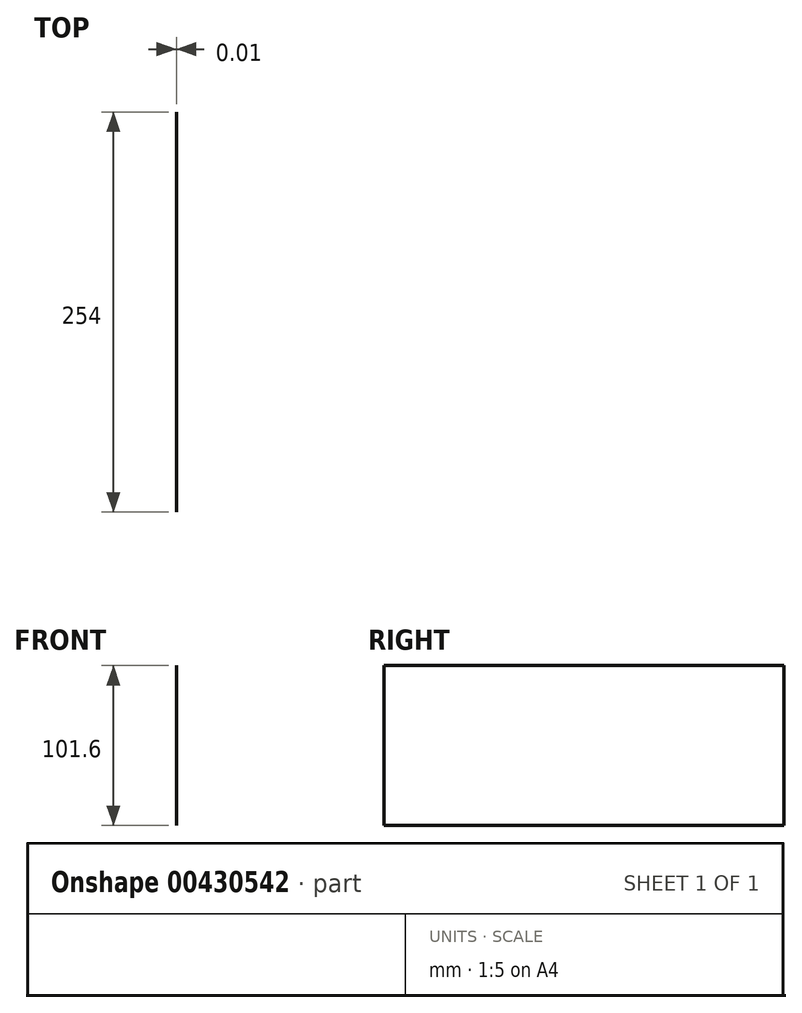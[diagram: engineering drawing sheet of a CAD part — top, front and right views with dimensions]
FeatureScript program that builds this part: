
annotation { "Feature Type Name" : "Feature", "Feature Type Description" : "" }
export const myFeature = defineFeature(function(context is Context, id is Id, definition is map)
    precondition{}
    {
        {
            var Q0;
            Q0=qCreatedBy(makeId("Right.planeOp"),FACE);
            var sketch = newSketch(context, id + "F0", { "sketchPlane" : qUnion([Q0])});
            skLineSegment(sketch, "E0.bottom", {"start": v(-109.97, 63.47) * mm, "end": v(144.03, 63.47) * mm});
            skLineSegment(sketch, "E0.top", {"start": v(-109.97, -38.13) * mm, "end": v(144.03, -38.13) * mm});
            skLineSegment(sketch, "E0.left", {"start": v(-109.97, 63.47) * mm, "end": v(-109.97, -38.13) * mm});
            skLineSegment(sketch, "E0.right", {"start": v(144.03, 63.47) * mm, "end": v(144.03, -38.13) * mm});
            skSolve(sketch);
        }
        {
            var Q0;
            Q0=makeQuery(id+"F0.imprint","IMPRINT",FACE,{"disambiguationData":[TD([[makeQuery(id+"F0.imprint","IMPRINT",EDGE,{"derivedFrom":sQuery(id+"F0.wireOp",EDGE,"E0.bottom")}),-1.0]])]});
            extrude(context, id + "F1", {"entities" : qUnion([Q0]), "depth" : 3 / 406.4 * mm});
        }
    });
